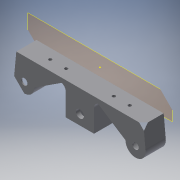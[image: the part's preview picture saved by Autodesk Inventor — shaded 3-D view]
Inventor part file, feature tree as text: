
AUTODESK INVENTOR PART (.ipt)
format: ipt  version: 2016 (Build 200138000, 138)  size: 217,088 bytes
history: native  units: in
note: dims shown in document units (in); Inventor stores cm internally (conversion verified against a paired STEP export)
features: reference x9, sketch x6, extrude x5, fillet x2, plane x1, chamfer x1
ambient origin geometry x8: Origin, YZ Plane, XZ Plane, XY Plane, X Axis, Y Axis, Z Axis, Center Point
bodies: Solid1 (feature_tree)
feature tree (24):
  plane  "Work Plane1"
  extrude  "Extrusion1"  Depth=1.4in
  extrude  "Extrusion2"  Depth=1.0in TaperAngle=0.0deg
  extrude  "Extrusion3"  Depth=0.9449in
  fillet  "Fillet1"  Radius=0.9449in
  extrude  "Extrusion4"  Depth=0.4in
  chamfer  "Chamfer1"  Distance=0.85in
  fillet  "Fillet2"  Radius=0.85in
  sketch  "Sketch5"  dims[d13=0.4in]
  extrude  "Extrusion5"  Depth=0.14in
  sketch  "Sketch1"  dims[d0=0.4in d2=1.4in]
  reference  "Reference1"
  reference  "Reference2"
  reference  "Reference3"
  reference  "Reference4"
  sketch  "Sketch2"  dims[d3=1.0in d5=1.0in d6=0.0in]
  reference  "Reference5"
  reference  "Reference6"
  sketch  "Sketch3"  dims[d7=0.5906in d8=0.5906in d9=0.9449in d10=0.0in]
  sketch  "Sketch4"  dims[d11=0.2in d12=0.4in]
  reference  "Reference7"
  sketch  "Sketch6"  dims[d14=0.425in d15=0.85in d16=0.85in d17=0.14in d18=0.4in d19=0.1in d20=0.85in d21=0.0in d22=0.425in d23=1.1811in d24=0.7874in d25=0.1575in d26=0.1575in d27=1.0in d28=0.0in d29=0.125in d30=0.125in d31=45.0deg d32=0.3in d33=0.2in d34=0.0in]
  reference  "Reference8"
  reference  "Reference9"
